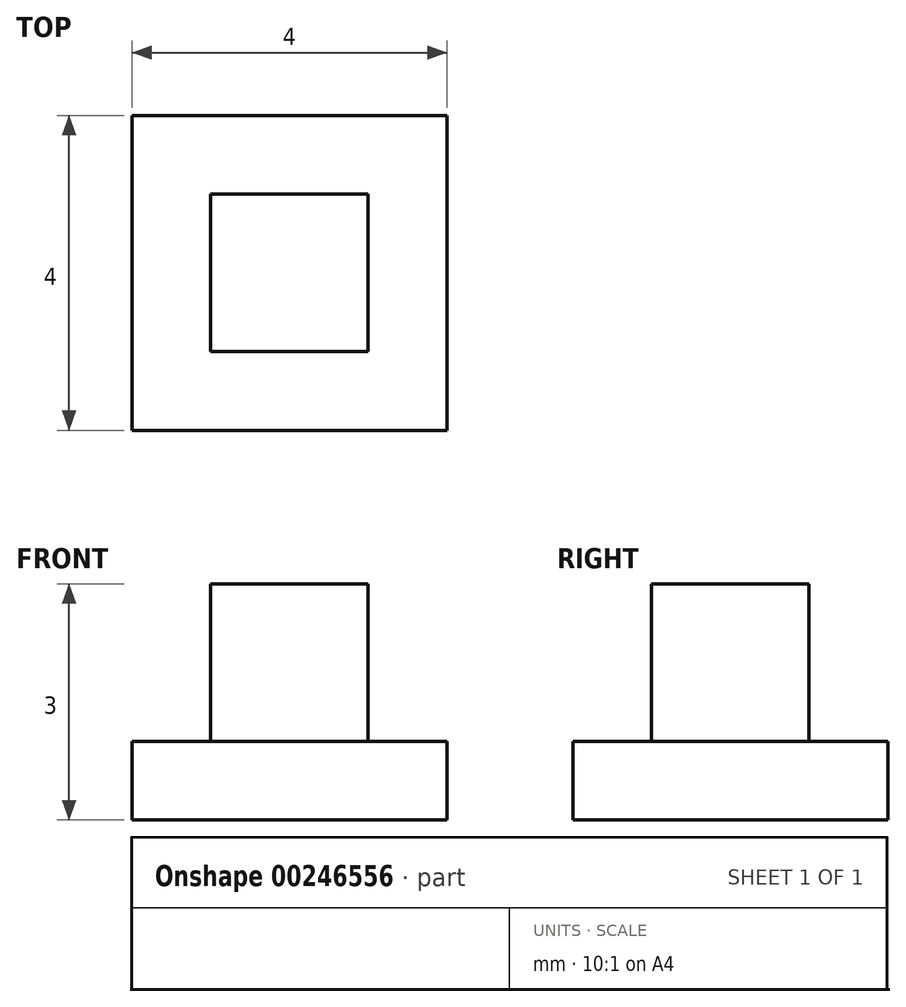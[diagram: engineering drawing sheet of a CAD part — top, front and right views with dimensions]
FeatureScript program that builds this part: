
annotation { "Feature Type Name" : "Feature", "Feature Type Description" : "" }
export const myFeature = defineFeature(function(context is Context, id is Id, definition is map)
    precondition{}
    {
        {
            var Q0;
            Q0=qCreatedBy(makeId("Top.planeOp"),FACE);
            var sketch = newSketch(context, id + "F0", { "sketchPlane" : qUnion([Q0])});
            skLineSegment(sketch, "E0.bottom", {"start": v(0, 4) * mm, "end": v(4, 4) * mm});
            skLineSegment(sketch, "E0.top", {"start": v(0, 0) * mm, "end": v(4, 0) * mm});
            skLineSegment(sketch, "E0.left", {"start": v(0, 4) * mm, "end": v(0, 0) * mm});
            skLineSegment(sketch, "E0.right", {"start": v(4, 4) * mm, "end": v(4, 0) * mm});
            skSolve(sketch);
        }
        {
            var Q0;
            Q0=makeQuery(id+"F0.imprint","IMPRINT",FACE,{"disambiguationData":[TD([[makeQuery(id+"F0.imprint","IMPRINT",EDGE,{"derivedFrom":sQuery(id+"F0.wireOp",EDGE,"E0.bottom")}),-1.0]])]});
            extrude(context, id + "F1", {"entities" : qUnion([Q0]), "depth" : 1 * mm});
        }
        {
            var Q0;
            Q0=makeQuery(id+"F1.opExtrude","CAP_FACE",FACE,{"disambiguationData":[OSD([sQuery(id+"F0.wireOp",EDGE,"E0.bottom"),sQuery(id+"F0.wireOp",EDGE,"E0.top"),sQuery(id+"F0.wireOp",EDGE,"E0.left"),sQuery(id+"F0.wireOp",EDGE,"E0.right")])],"isStart":false});
            var sketch = newSketch(context, id + "F2", { "sketchPlane" : qUnion([Q0])});
            skLineSegment(sketch, "E1", {"start": v(2, 4) * mm, "end": v(2, 0) * mm, "construction": true});
            skLineSegment(sketch, "E2.bottom", {"start": v(1, 3) * mm, "end": v(3, 3) * mm});
            skLineSegment(sketch, "E2.top", {"start": v(1, 1) * mm, "end": v(3, 1) * mm});
            skLineSegment(sketch, "E2.left", {"start": v(1, 3) * mm, "end": v(1, 1) * mm});
            skLineSegment(sketch, "E2.right", {"start": v(3, 3) * mm, "end": v(3, 1) * mm});
            skSolve(sketch);
        }
        {
            var Q0;
            Q0=makeQuery(id+"F2.imprint","IMPRINT",FACE,{"disambiguationData":[TD([[makeQuery(id+"F2.imprint","IMPRINT",EDGE,{"derivedFrom":sQuery(id+"F2.wireOp",EDGE,"E2.bottom")}),-1.0]])]});
            extrude(context, id + "F3", {"entities" : qUnion([Q0]), "operationType" : NewBodyOperationType.ADD, "depth" : 2 * mm});
        }
    });
